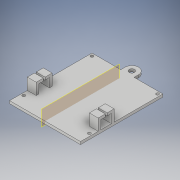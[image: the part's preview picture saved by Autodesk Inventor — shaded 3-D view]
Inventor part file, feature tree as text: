
AUTODESK INVENTOR PART (.ipt)
format: ipt  version: 2018 (Build 220112000, 112)  size: 177,152 bytes
history: native  units: mm
features: extrude x4, sketch x4, mirror x2, plane x1
ambient origin geometry x8: Origin, YZ Plane, XZ Plane, XY Plane, X Axis, Y Axis, Z Axis, Center Point
bodies: Solid1 (feature_tree)
feature tree (11):
  extrude  "Extrusion1"  Depth=93.0mm
  sketch  "Sketch3"  dims[d2=3.0mm d3=0.0mm d4=3.0mm]
  plane  "Work Plane1"
  extrude  "Extrusion2"  Depth=3.0mm
  mirror  "Mirror1"
  extrude  "Extrusion3"  Depth=20.0mm
  mirror  "Mirror2"
  extrude  "Extrusion4"  Depth=10.0mm
  sketch  "Sketch1"  dims[d0=80.0mm d1=93.0mm]
  sketch  "Sketch4"  dims[d5=3.0mm d6=20.0mm]
  sketch  "Sketch5"  dims[d7=12.0mm d8=10.0mm d9=3.0mm d10=5.0mm d11=5.0mm d12=3.0mm d13=10.0mm d14=0.0mm d15=3.2mm d16=3.0mm d17=13.0mm d18=3.0mm d19=10.0mm d20=0.0mm d21=6.0mm d22=15.0mm d23=5.0mm d24=3.0mm d25=0.0mm]
